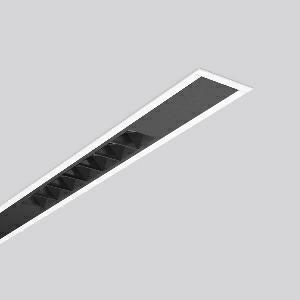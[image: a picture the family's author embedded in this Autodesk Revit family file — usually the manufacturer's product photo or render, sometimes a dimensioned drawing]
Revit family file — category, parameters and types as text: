
# Revit family: less_is_more_beamline_312465_002_0741
name_source: partatom
category: Lighting Fixtures
units: mm (PartAtom-declared; Revit-internal decimal feet)

## family parameters
Cut with Voids When Loaded = No
Host = Face
Light Source = No
Part Type = Normal
Room Calculation Point = No
Round Connector Dimension = Use Diameter
Shared = No

## types (1)
- LESS IS MORE BEAMLINE (1 x LED Modul 930, 1025 lm, 3000)
    Apparent Load = 23 VA
    CIE Flux Codes = 100 100 100 100 100
    Color Rendering = 90
    Color Temperature = 3000
    Default Elevation = 1800 mm
    Description = Series: LESS IS MORE BEAMLINE
Linear recessed ceiling and wall luminaire for aesthetically sophisticated lighting. Luminaire with two LED light units. Housing: extruded aluminium profile, powder-coated. End cap aluminium powder-coated. LED light unit with MRS technology: Mini-Reflector-System made of metallised thermoplastic with prismatic black glare-suppressing frame for pleasant glare-free light (RUG < 10). Each LED light unit has 7 reflector elements. Narrow beam light distribution. Ceiling installation with pre-assembled SBS mounting system. LED unit with integrated converter interchangeable and removable. Suitable for through-wiring. 
Colour: traffic white, matt (RAL 9016)
Length: 1141 mm
Width: 71 mm
Height: 1.5 mm
Cut-out length: 1128 mm
Cut-out width: 60 mm
Recess height: 125 mm
Luminaire: recess height: 106 mm
Lamp: LED
Socket: without socket
Colour temperature: 3000K
Colour rendering index (CRI): 90
System power: 23 W
Rated luminous flux: 2050 lm
Luminous efficiency: 89 lm/W
Control gear: Regulated power supply
Protection class: I
Type of protection: IP 20
    Height = 0 mm  [stored 0 ft]
    Lamp = 1 x LED Modul 930
    Lamp Light Flux = 1025 lm
    Lamp count = 1
    Length = 1141 mm
    Lifetime = 50000 h
    Luminous efficacy = 89 lm/W
    Manufacturer = RZB
    ModVariant = No
    Model = 312465.002
    Mounting Place = Ceiling, Wall
    Mounting Type = Recessed
    Number of Poles = 1
    OnlyDefault = Yes
    Power Factor = 1
    Product Name = LESS IS MORE BEAMLINE
    Product group = Recessed LED linear luminaires
    ProductGroupID = 407
    Protection Class = Protection class I
    Protection Degree = IP 20
    RLX_Detail_Level = 1
    RLX_Emergency_Light_Flux = 0 lm
    RLX_Emergency_Type = 0
    RLX_Emergency_Type_DB = No
    RlxData = <blob elided: 23717 chars, md5=abfb2222>
    Socket = socket
    Standby Power = 0 W
    System Light Flux = 2050 lm
    System Power = 23 W
    Type Comments = Product without accessories
    Type Image = 312465.002.jpg
    URL = http://relux.com
    VarID = ---
    Voltage = 230 V
    Voltage Range = 220-240 V
    Weight = 0.00 kg
    Width = 71 mm

note: [stored X ft] marks values corroborated as IEEE doubles in the binary element streams (Revit-internal decimal feet)

## geometry (parser evidence)
native form markers: Blend x4, Sweep x15
no freeform markers — native parametric forms only
